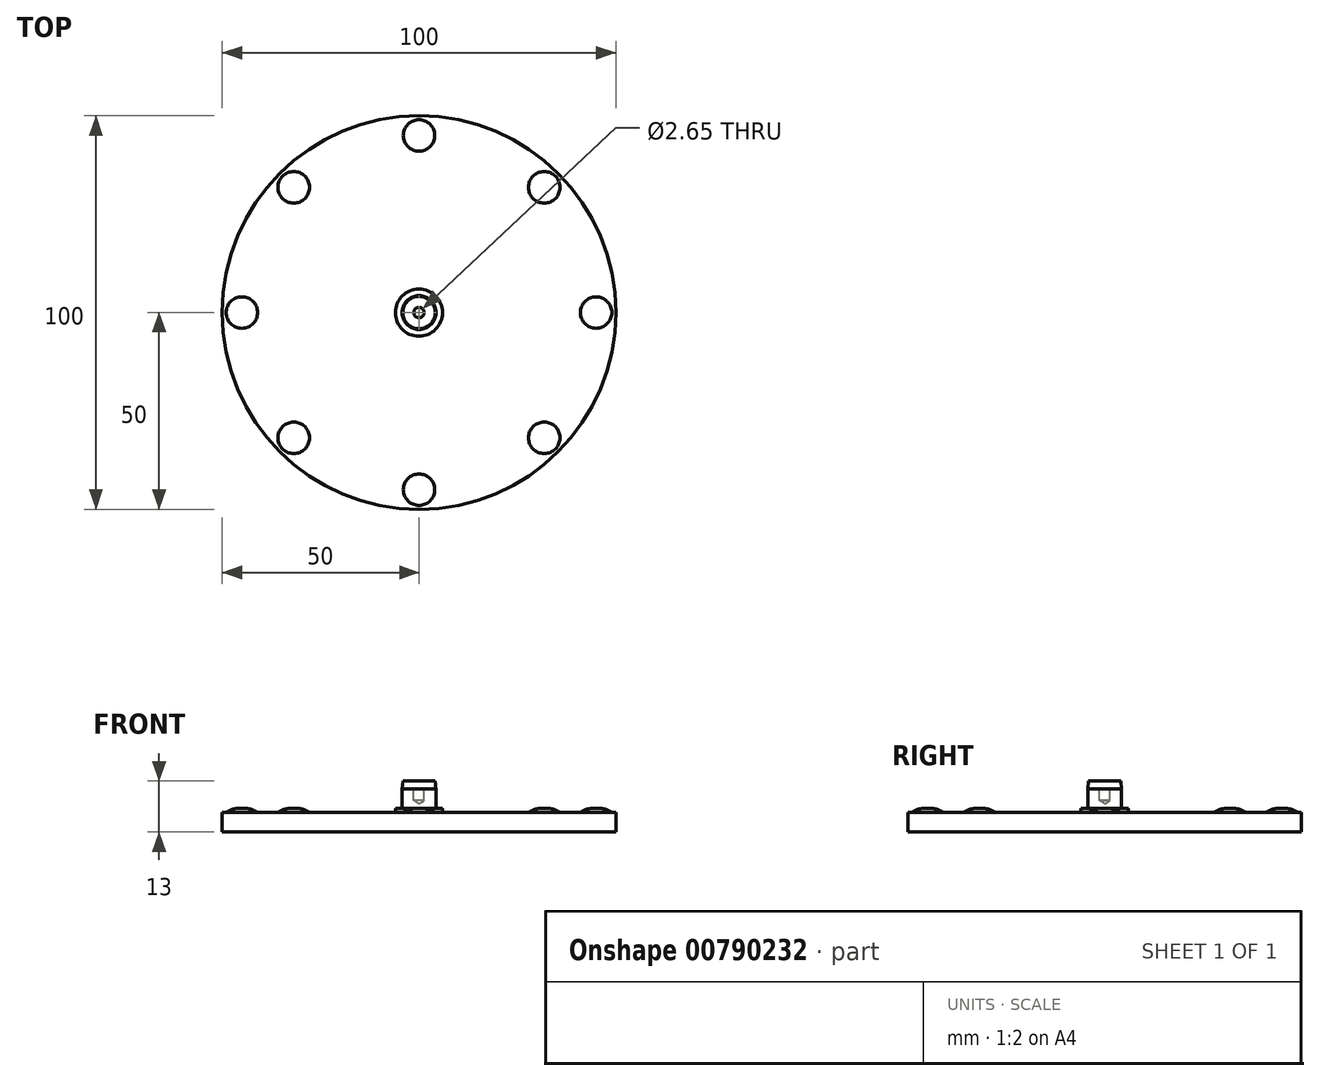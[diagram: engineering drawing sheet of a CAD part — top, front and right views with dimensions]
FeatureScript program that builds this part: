
annotation { "Feature Type Name" : "Feature", "Feature Type Description" : "" }
export const myFeature = defineFeature(function(context is Context, id is Id, definition is map)
    precondition{}
    {
        {
            var Q0;
            Q0=qCreatedBy(makeId("Top.planeOp"),FACE);
            var sketch = newSketch(context, id + "F0", { "sketchPlane" : qUnion([Q0])});
            skCircle(sketch, "E0", {"center": v(0, 0) * mm, "radius": 50 * mm});
            skSolve(sketch);
        }
        {
            var Q0;
            Q0 = qSketchRegion(id + "F0", true);
            extrude(context, id + "F1", {"entities" : qUnion([Q0]), "depth" : 5 * mm, "offsetDistance" : 25 * mm});
        }
        {
            var Q0;
            Q0=makeQuery(id+"F1.opExtrude","CAP_FACE",FACE,{"disambiguationData":[OSD([sQuery(id+"F0.wireOp",EDGE,"E0")])],"isStart":false});
            var sketch = newSketch(context, id + "F2", { "sketchPlane" : qUnion([Q0])});
            skCircle(sketch, "E1", {"center": v(0, 0) * mm, "radius": 6 * mm});
            skSolve(sketch);
        }
        {
            var Q0;
            Q0 = qSketchRegion(id + "F2", true);
            extrude(context, id + "F3", {"entities" : qUnion([Q0]), "operationType" : NewBodyOperationType.ADD, "depth" : 1 * mm, "offsetDistance" : 25 * mm});
        }
        {
            var Q0;
            Q0=makeQuery(id+"F3.opExtrude","CAP_FACE",FACE,{"disambiguationData":[OSD([sQuery(id+"F2.wireOp",EDGE,"E1")])],"isStart":false});
            var sketch = newSketch(context, id + "F4", { "sketchPlane" : qUnion([Q0])});
            skCircle(sketch, "E2", {"center": v(0, 0) * mm, "radius": 4.3 * mm});
            skSolve(sketch);
        }
        {
            var Q0;
            Q0 = qSketchRegion(id + "F4", true);
            extrude(context, id + "F5", {"entities" : qUnion([Q0]), "operationType" : NewBodyOperationType.ADD, "depth" : 7 * mm, "offsetDistance" : 25 * mm});
        }
        {
            var Q0;
            Q0=makeQuery(id+"F5.opExtrude","CAP_FACE",FACE,{"disambiguationData":[OSD([sQuery(id+"F4.wireOp",EDGE,"E2")])],"isStart":false});
            var sketch = newSketch(context, id + "F6", { "sketchPlane" : qUnion([Q0])});
            skPoint(sketch, "E3", {"position": v(0, 0) * mm});
            skSolve(sketch);
        }
        {
            var Q0;
            Q0=sQuery(id+"F6.wireOp",VERTEX,"E3");
            var Q1;
            Q1=makeQuery(id+"F1.opExtrude","SWEPT_BODY",BODY,{"disambiguationData":[OSD([sQuery(id+"F0.wireOp",EDGE,"E0")])]});
            hole(context, id + "F7", {"style" : HoleStyle.SIMPLE, "endStyle" : HoleEndStyle.BLIND, "holeDiameter" : 2.65 * mm, "majorDiameter" : 5 * mm, "holeDepth" : 5 * mm, "isTappedThrough" : true, "tappedDepth" : 12 * mm, "tapClearance" : 3, "startFromSketch" : true, "locations" : qUnion([Q0]), "scope" : qUnion([Q1])});
        }
        {
            var Q0;
            Q0=makeQuery(id+"F5.opExtrude","CAP_EDGE",EDGE,{"disambiguationData":[OSD([sQuery(id+"F4.wireOp",EDGE,"E2")])],"isStart":false});
            chamfer(context, id + "F8", {"entities" : qUnion([Q0]), "chamferType" : ChamferType.TWO_OFFSETS, "width1" : .2 * mm, "oppositeDirection" : false, "width2" : 2 * mm, "tangentPropagation" : true});
        }
        {
            var Q0;
            Q0=makeQuery(id+"F1.opExtrude","CAP_FACE",FACE,{"disambiguationData":[OSD([sQuery(id+"F0.wireOp",EDGE,"E0")])],"isStart":false});
            var sketch = newSketch(context, id + "F9", { "sketchPlane" : qUnion([Q0])});
            skCircle(sketch, "E4", {"center": v(0, 45) * mm, "radius": 4 * mm});
            skCircle(sketch, "E5.1.0", {"center": v(-31.82, 31.82) * mm, "radius": 4 * mm});
            skCircle(sketch, "E5.2.0", {"center": v(-45, 0) * mm, "radius": 4 * mm});
            skCircle(sketch, "E5.3.0", {"center": v(-31.82, -31.82) * mm, "radius": 4 * mm});
            skCircle(sketch, "E5.4.0", {"center": v(0, -45) * mm, "radius": 4 * mm});
            skCircle(sketch, "E5.5.0", {"center": v(31.82, -31.82) * mm, "radius": 4 * mm});
            skCircle(sketch, "E5.6.0", {"center": v(45, 0) * mm, "radius": 4 * mm});
            skCircle(sketch, "E5.7.0", {"center": v(31.82, 31.82) * mm, "radius": 4 * mm});
            skPoint(sketch, "E5.center", {"position": v(0, 0) * mm});
            skSolve(sketch);
        }
        {
            var Q0;
            Q0 = qSketchRegion(id + "F9", true);
            extrude(context, id + "F10", {"entities" : qUnion([Q0]), "operationType" : NewBodyOperationType.ADD, "depth" : 1 * mm, "offsetDistance" : 25 * mm});
        }
        {
            var Q0;
            Q0=makeQuery(id+"F10.opExtrude","CAP_FACE",FACE,{"disambiguationData":[OSD([sQuery(id+"F9.wireOp",EDGE,"E5.4.0")])],"isStart":false});
            var Q1;
            Q1=makeQuery(id+"F10.opExtrude","CAP_FACE",FACE,{"disambiguationData":[OSD([sQuery(id+"F9.wireOp",EDGE,"E5.5.0")])],"isStart":false});
            var Q2;
            Q2=makeQuery(id+"F10.opExtrude","CAP_FACE",FACE,{"disambiguationData":[OSD([sQuery(id+"F9.wireOp",EDGE,"E5.6.0")])],"isStart":false});
            var Q3;
            Q3=makeQuery(id+"F10.opExtrude","CAP_FACE",FACE,{"disambiguationData":[OSD([sQuery(id+"F9.wireOp",EDGE,"E5.7.0")])],"isStart":false});
            var Q4;
            Q4=makeQuery(id+"F10.opExtrude","CAP_FACE",FACE,{"disambiguationData":[OSD([sQuery(id+"F9.wireOp",EDGE,"E4")])],"isStart":false});
            var Q5;
            Q5=makeQuery(id+"F10.opExtrude","CAP_FACE",FACE,{"disambiguationData":[OSD([sQuery(id+"F9.wireOp",EDGE,"E5.1.0")])],"isStart":false});
            var Q6;
            Q6=makeQuery(id+"F10.opExtrude","CAP_FACE",FACE,{"disambiguationData":[OSD([sQuery(id+"F9.wireOp",EDGE,"E5.2.0")])],"isStart":false});
            var Q7;
            Q7=makeQuery(id+"F10.opExtrude","CAP_FACE",FACE,{"disambiguationData":[OSD([sQuery(id+"F9.wireOp",EDGE,"E5.3.0")])],"isStart":false});
            fillet(context, id + "F11", {"entities" : qUnion([Q0, Q1, Q2, Q3, Q4, Q5, Q6, Q7]), "radius" : 5 * mm, "tangentPropagation" : true, "allowEdgeOverflow" : false});
        }
    });
